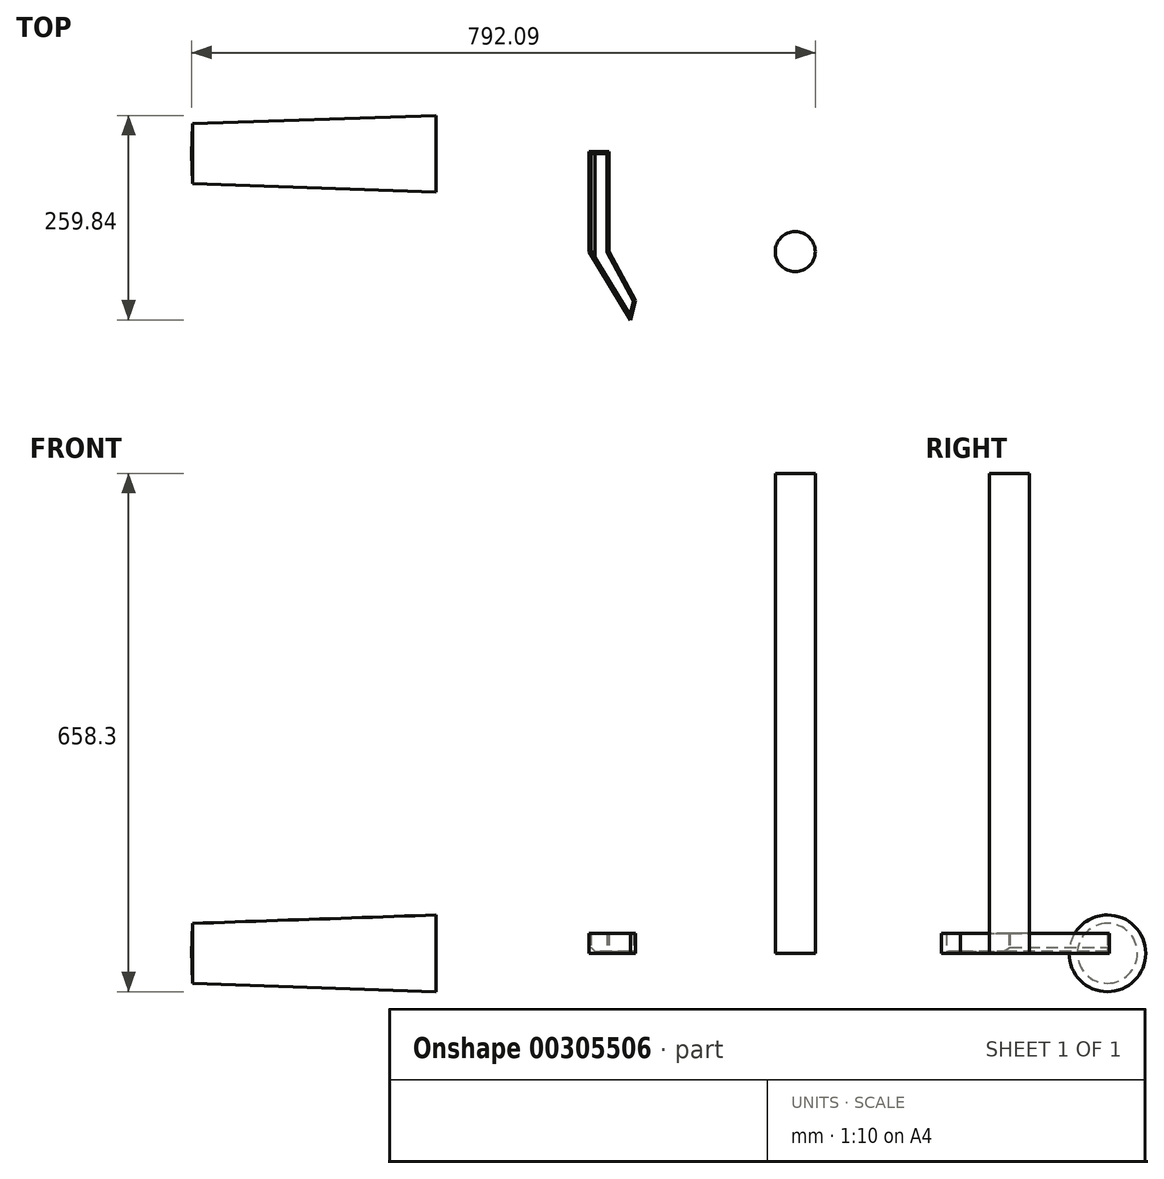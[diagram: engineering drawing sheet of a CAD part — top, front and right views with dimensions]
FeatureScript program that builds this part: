
annotation { "Feature Type Name" : "Feature", "Feature Type Description" : "" }
export const myFeature = defineFeature(function(context is Context, id is Id, definition is map)
    precondition{}
    {
        {
            var Q0;
            Q0=qCreatedBy(makeId("Top.planeOp"),FACE);
            var sketch = newSketch(context, id + "F0", { "sketchPlane" : qUnion([Q0])});
            skCircle(sketch, "E0", {"center": v(0, 0) * mm, "radius": 25.4 * mm});
            skSolve(sketch);
        }
        {
            var Q0;
            Q0 = qSketchRegion(id + "F0", true);
            extrude(context, id + "F1", {"entities" : qUnion([Q0]), "depth" : 609.6 * mm});
        }
        {
            var Q0;
            Q0=qCreatedBy(makeId("Top.planeOp"),FACE);
            var sketch = newSketch(context, id + "F2", { "sketchPlane" : qUnion([Q0])});
            skLineSegment(sketch, "E1", {"start": v(-209.06, -86.75) * mm, "end": v(-261.94, 0) * mm});
            skLineSegment(sketch, "E2", {"start": v(-261.94, 0) * mm, "end": v(-261.94, 25.4) * mm});
            skLineSegment(sketch, "E3", {"start": v(-261.94, 25.4) * mm, "end": v(-261.94, 127) * mm});
            skLineSegment(sketch, "E4", {"start": v(-261.94, 127) * mm, "end": v(-236.54, 127) * mm});
            skLineSegment(sketch, "E5", {"start": v(-236.54, 127) * mm, "end": v(-236.54, 0) * mm});
            skLineSegment(sketch, "E6", {"start": v(-236.54, 0) * mm, "end": v(-203.04, -62.08) * mm});
            skLineSegment(sketch, "E7", {"start": v(-203.04, -62.08) * mm, "end": v(-209.06, -86.75) * mm});
            skSolve(sketch);
        }
        {
            var Q0;
            Q0=makeQuery(id+"F2.imprint","IMPRINT",FACE,{"disambiguationData":[TD([[makeQuery(id+"F2.imprint","IMPRINT",EDGE,{"derivedFrom":sQuery(id+"F2.wireOp",EDGE,"E1")}),-1.0]])]});
            var Q1;
            Q1 = qSketchRegion(id + "F2", true);
            extrude(context, id + "F3", {"entities" : qUnion([Q0, Q1]), "depth" : 25.4 * mm});
        }
        {
            var Q0;
            Q0=makeQuery(id+"F3.opExtrude","CAP_FACE",FACE,{"disambiguationData":[OSD([sQuery(id+"F2.wireOp",EDGE,"E1"),sQuery(id+"F2.wireOp",EDGE,"E2"),sQuery(id+"F2.wireOp",EDGE,"E3"),sQuery(id+"F2.wireOp",EDGE,"E4"),sQuery(id+"F2.wireOp",EDGE,"E5"),sQuery(id+"F2.wireOp",EDGE,"E6"),sQuery(id+"F2.wireOp",EDGE,"E7")])],"isStart":false});
            shell(context, id + "F4", {"entities" : qUnion([Q0]), "thickness" : 2.54 * mm});
        }
        {
            var Q0;
            {var subQ0=sQuery(id+"F2.wireOp",EDGE,"E3");var subQ1=sQuery(id+"F2.wireOp",EDGE,"E2");Q0=makeQuery(id+"F4.opShell","OFFSET_EDGE",EDGE,{"disambiguationData":[OSD([subQ1,subQ0]),TDD([makeQuery(id+"F3.opExtrude","CAP_EDGE",EDGE,{"disambiguationData":[OSD([subQ1,subQ0])],"isStart":true})])]});}
            chamfer(context, id + "F5", {"entities" : qUnion([Q0]), "width" : 5.08 * mm, "tangentPropagation" : true});
        }
        {
            var Q0;
            Q0=qCreatedBy(makeId("Top.planeOp"),FACE);
            var sketch = newSketch(context, id + "F6", { "sketchPlane" : qUnion([Q0])});
            skLineSegment(sketch, "E8", {"start": v(-424.58, 320.4) * mm, "end": v(-303.4, 297.82) * mm});
            skLineSegment(sketch, "E9", {"start": v(-303.4, 297.82) * mm, "end": v(-367.56, 240.8) * mm});
            skLineSegment(sketch, "E10", {"start": v(-367.56, 240.8) * mm, "end": v(-487.53, 262.19) * mm});
            skLineSegment(sketch, "E11", {"start": v(-487.53, 262.19) * mm, "end": v(-424.58, 320.4) * mm});
            skLineSegment(sketch, "E12", {"start": v(-766.69, 124.39) * mm, "end": v(-456.05, 124.39) * mm});
            skPoint(sketch, "E12.endSnap0", {"position": v(-456.05, 291.29) * mm});
            skLineSegment(sketch, "E13", {"start": v(-456.05, 124.39) * mm, "end": v(-456.05, 75.69) * mm});
            skLineSegment(sketch, "E14", {"start": v(-456.05, 75.69) * mm, "end": v(-765.5, 86.38) * mm});
            skLineSegment(sketch, "E15", {"start": v(-765.5, 86.38) * mm, "end": v(-766.69, 124.39) * mm});
            skSolve(sketch);
        }
        {
            var Q0;
            Q0=makeQuery(id+"F6.imprint","IMPRINT",FACE,{"disambiguationData":[TD([[makeQuery(id+"F6.imprint","IMPRINT",EDGE,{"derivedFrom":sQuery(id+"F6.wireOp",EDGE,"E12")}),-1.0]])]});
            var Q1;
            Q1=sQuery(id+"F6.wireOp",EDGE,"E12");
            revolve(context, id + "F7", {"entities" : qUnion([Q0]), "axis" : qUnion([Q1]), "revolveType" : RevolveType.FULL});
        }
    });
